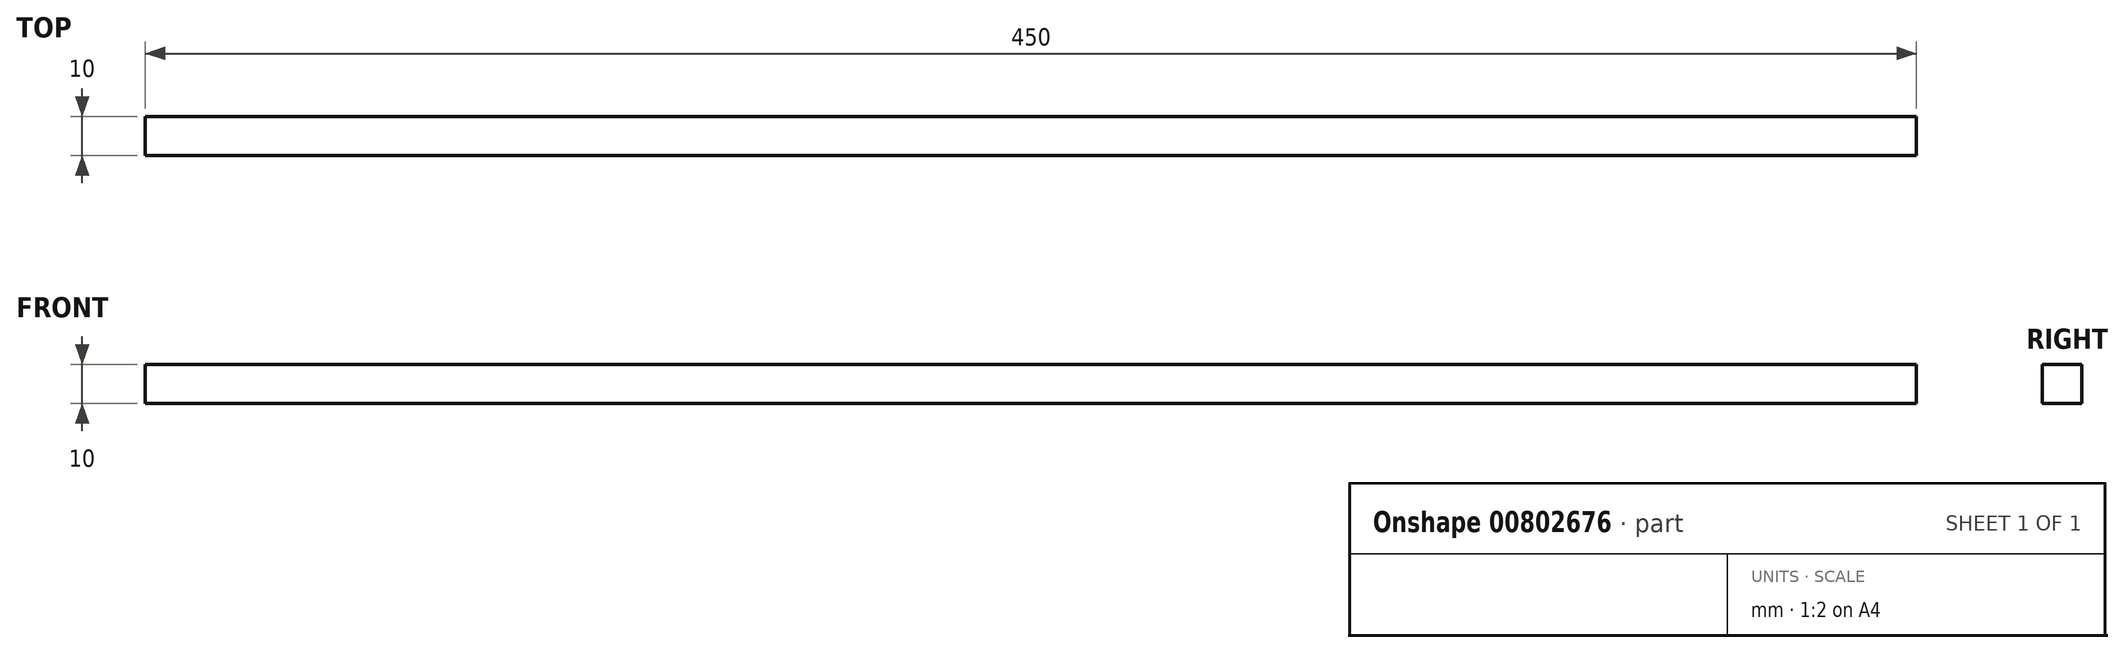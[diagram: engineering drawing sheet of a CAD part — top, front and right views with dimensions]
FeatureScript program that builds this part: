
annotation { "Feature Type Name" : "Feature", "Feature Type Description" : "" }
export const myFeature = defineFeature(function(context is Context, id is Id, definition is map)
    precondition{}
    {
        {
            var Q0;
            Q0=qCreatedBy(makeId("Right.planeOp"),FACE);
            var sketch = newSketch(context, id + "F0", { "sketchPlane" : qUnion([Q0])});
            skLineSegment(sketch, "E0.bottom", {"start": v(0, 0) * mm, "end": v(10, 0) * mm});
            skLineSegment(sketch, "E0.top", {"start": v(0, 10) * mm, "end": v(10, 10) * mm});
            skLineSegment(sketch, "E0.left", {"start": v(0, 0) * mm, "end": v(0, 10) * mm});
            skLineSegment(sketch, "E0.right", {"start": v(10, 0) * mm, "end": v(10, 10) * mm});
            skSolve(sketch);
        }
        {
            var Q0;
            Q0=makeQuery(id+"F0.imprint","IMPRINT",FACE,{"disambiguationData":[TD([[makeQuery(id+"F0.imprint","IMPRINT",EDGE,{"derivedFrom":sQuery(id+"F0.wireOp",EDGE,"E0.bottom")}),1.0]])]});
            extrude(context, id + "F1", {"entities" : qUnion([Q0]), "depth" : 450 * mm, "offsetDistance" : 25 * mm});
        }
    });
